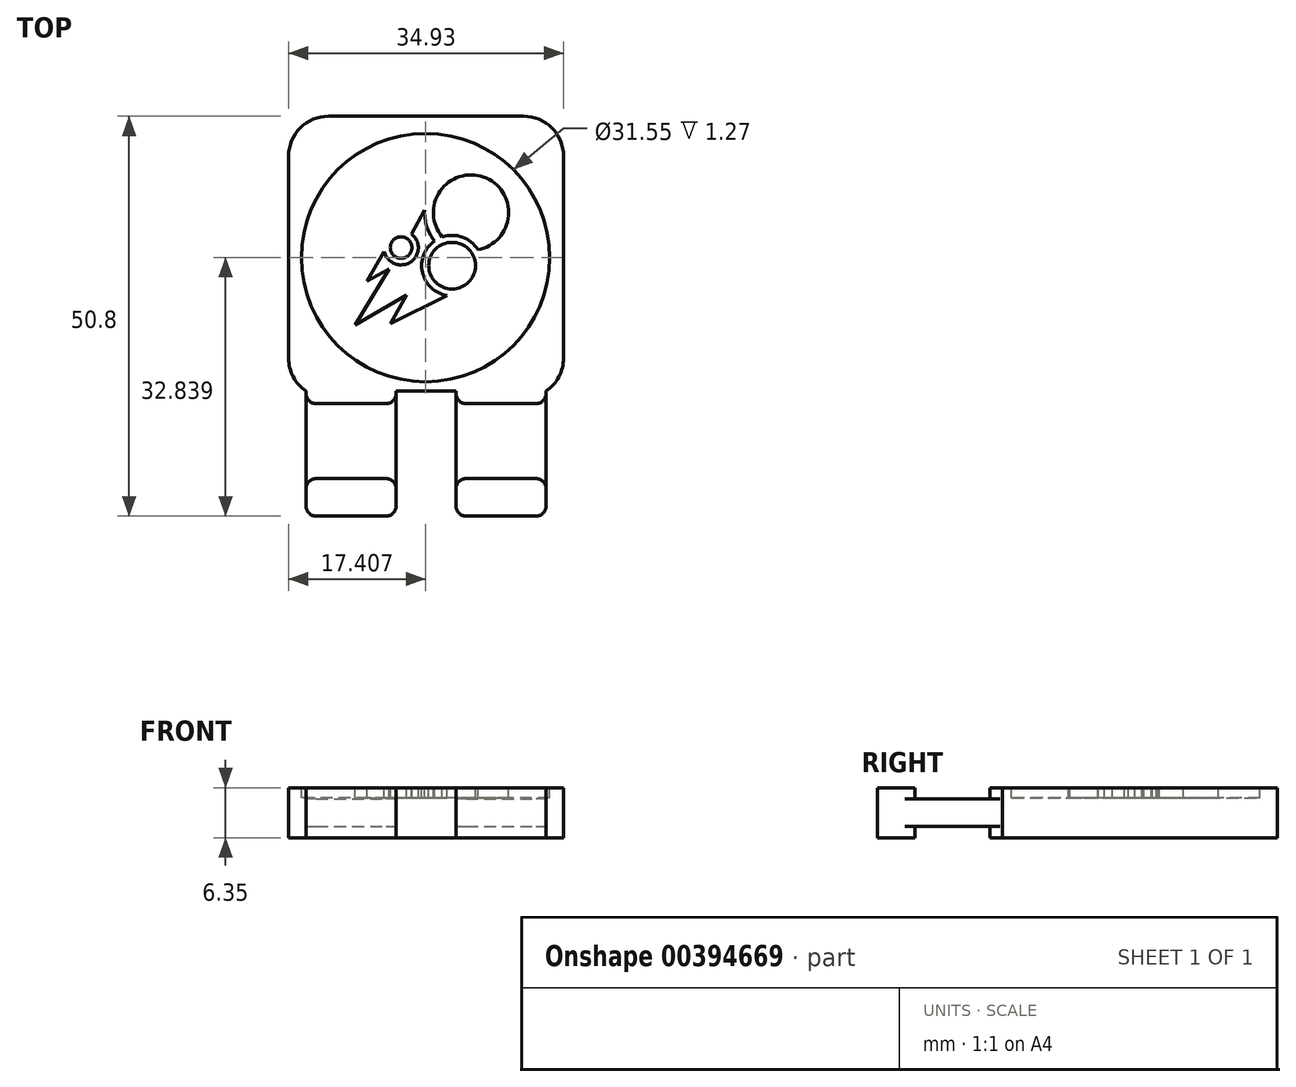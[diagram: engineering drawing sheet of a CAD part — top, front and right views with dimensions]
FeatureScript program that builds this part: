
annotation { "Feature Type Name" : "Feature", "Feature Type Description" : "" }
export const myFeature = defineFeature(function(context is Context, id is Id, definition is map)
    precondition{}
    {
        {
            var Q0;
            Q0=qCreatedBy(makeId("Top.planeOp"),FACE);
            var sketch = newSketch(context, id + "F0", { "sketchPlane" : qUnion([Q0])});
            skLineSegment(sketch, "E0.bottom", {"start": v(-17.15, 21.98) * mm, "end": v(17.78, 21.98) * mm});
            skLineSegment(sketch, "E0.top", {"start": v(-14.92, -28.82) * mm, "end": v(-3.5, -28.82) * mm});
            skLineSegment(sketch, "E0.left", {"start": v(-17.15, 21.98) * mm, "end": v(-17.15, -12.94) * mm});
            skLineSegment(sketch, "E0.right", {"start": v(17.78, 21.98) * mm, "end": v(17.78, -12.94) * mm});
            skPoint(sketch, "E0.middle", {"position": v(0, 0) * mm});
            skLineSegment(sketch, "E1", {"start": v(-17.15, -12.94) * mm, "end": v(-14.92, -12.94) * mm});
            skLineSegment(sketch, "E2", {"start": v(-14.92, -12.94) * mm, "end": v(-14.92, -28.82) * mm});
            skLineSegment(sketch, "E3", {"start": v(-3.5, -28.82) * mm, "end": v(-3.5, -12.94) * mm});
            skLineSegment(sketch, "E4", {"start": v(-3.5, -12.94) * mm, "end": v(4.13, -12.94) * mm});
            skLineSegment(sketch, "E5", {"start": v(4.13, -12.94) * mm, "end": v(4.13, -28.82) * mm});
            skLineSegment(sketch, "E6", {"start": v(17.78, -12.94) * mm, "end": v(15.56, -12.94) * mm});
            skLineSegment(sketch, "E7", {"start": v(15.56, -12.94) * mm, "end": v(15.56, -28.82) * mm});
            skLineSegment(sketch, "E8.trimOffspring", {"start": v(4.13, -28.82) * mm, "end": v(15.56, -28.82) * mm});
            skSolve(sketch);
        }
        {
            var Q0;
            Q0 = qSketchRegion(id + "F0", true);
            extrude(context, id + "F1", {"entities" : qUnion([Q0]), "endBound" : BoundingType.SYMMETRIC, "depth" : 6.35 * mm});
        }
        {
            var Q0;
            Q0=qCreatedBy(makeId("Right.planeOp"),FACE);
            var sketch = newSketch(context, id + "F2", { "sketchPlane" : qUnion([Q0])});
            skLineSegment(sketch, "E9", {"start": v(-14.53, -1.73) * mm, "end": v(-24.05, -1.73) * mm});
            skLineSegment(sketch, "E10", {"start": v(-24.05, -1.73) * mm, "end": v(-24.05, -3.18) * mm});
            skLineSegment(sketch, "E11", {"start": v(-24.05, -3.18) * mm, "end": v(-14.53, -3.18) * mm});
            skLineSegment(sketch, "E12", {"start": v(-14.53, 1.73) * mm, "end": v(-24.05, 1.73) * mm});
            skLineSegment(sketch, "E13", {"start": v(-24.05, 1.73) * mm, "end": v(-24.05, 3.18) * mm});
            skLineSegment(sketch, "E14", {"start": v(-24.05, 3.18) * mm, "end": v(-14.53, 3.18) * mm});
            skLineSegment(sketch, "E15", {"start": v(-14.53, 1.73) * mm, "end": v(-14.53, 3.18) * mm});
            skLineSegment(sketch, "E16", {"start": v(-14.53, -3.18) * mm, "end": v(-14.53, -1.73) * mm});
            skSolve(sketch);
        }
        {
            var Q0;
            Q0 = qSketchRegion(id + "F2", true);
            extrude(context, id + "F3", {"entities" : qUnion([Q0]), "operationType" : NewBodyOperationType.REMOVE, "endBound" : BoundingType.SYMMETRIC, "oppositeDirection" : true, "depth" : 50.8 * mm});
        }
        {
            var Q0;
            {var subQ0=sQuery(id+"F0.wireOp",EDGE,"E1");var subQ1=sQuery(id+"F0.wireOp",EDGE,"E0.left");var subQ2=sQuery(id+"F0.wireOp",EDGE,"E0.right");var subQ3=sQuery(id+"F0.wireOp",EDGE,"E0.bottom");var subQ4=sQuery(id+"F0.wireOp",EDGE,"E6");var subQ5=sQuery(id+"F0.wireOp",EDGE,"E4");Q0=makeQuery(id+"F3.boolean.opBoolean","SPLIT",FACE,{"disambiguationData":[TD([makeQuery(id+"F1.opExtrude","SWEPT_FACE",FACE,{"disambiguationData":[OSD([subQ3])]})])],"derivedFrom":makeQuery(id+"F1.opExtrude","CAP_FACE",FACE,{"disambiguationData":[OSD([subQ3,sQuery(id+"F0.wireOp",EDGE,"E0.top"),subQ1,subQ2,subQ0,sQuery(id+"F0.wireOp",EDGE,"E2"),sQuery(id+"F0.wireOp",EDGE,"E3"),subQ5,sQuery(id+"F0.wireOp",EDGE,"E5"),subQ4,sQuery(id+"F0.wireOp",EDGE,"E7"),sQuery(id+"F0.wireOp",EDGE,"E8.trimOffspring")])],"isStart":false})});}
            var sketch = newSketch(context, id + "F4", { "sketchPlane" : qUnion([Q0])});
            skPoint(sketch, "E17", {"position": v(-17.15, 4.52) * mm});
            skArc(sketch, "E18", {"start": v(6.9, 5.03) * mm, "mid": v(7.65, 14.25) * mm, "end": v(2.38, 6.65) * mm});
            skCircle(sketch, "E19", {"center": v(3.62, 3) * mm, "radius": 2.97 * mm});
            skCircle(sketch, "E20", {"center": v(-2.86, 5.3) * mm, "radius": 1.37 * mm});
            skArc(sketch, "E21", {"start": v(0.15, 10.05) * mm, "mid": v(0.4, 7.98) * mm, "end": v(1.38, 6.13) * mm});
            skArc(sketch, "E22", {"start": v(6.9, 5.03) * mm, "mid": v(4.92, 6.62) * mm, "end": v(2.38, 6.65) * mm});
            skArc(sketch, "E23", {"start": v(-5, 4.82) * mm, "mid": v(-1.68, 3.44) * mm, "end": v(-1.5, 7.03) * mm});
            skLineSegment(sketch, "E24", {"start": v(-7.2, 1.03) * mm, "end": v(-5, 4.82) * mm});
            skLineSegment(sketch, "E25", {"start": v(-7.2, 1.03) * mm, "end": v(-4.38, 2.58) * mm});
            skLineSegment(sketch, "E26", {"start": v(-4.38, 2.58) * mm, "end": v(-8.68, -4.53) * mm});
            skLineSegment(sketch, "E27", {"start": v(-8.68, -4.53) * mm, "end": v(-2.16, -0.76) * mm});
            skLineSegment(sketch, "E28", {"start": v(-2.16, -0.76) * mm, "end": v(-4.22, -4.33) * mm});
            skLineSegment(sketch, "E29", {"start": v(-4.22, -4.33) * mm, "end": v(2.95, -0.8) * mm});
            skLineSegment(sketch, "E30.trimOffspring", {"start": v(-1.5, 7.03) * mm, "end": v(0.15, 10.05) * mm});
            skArc(sketch, "E31.trimOffspring", {"start": v(1.38, 6.13) * mm, "mid": v(-0.14, 2.14) * mm, "end": v(2.95, -0.8) * mm});
            skLineSegment(sketch, "E32", {"start": v(-17.15, 21.98) * mm, "end": v(17.78, 21.98) * mm});
            skLineSegment(sketch, "E33", {"start": v(17.78, 21.98) * mm, "end": v(17.78, -12.94) * mm});
            skLineSegment(sketch, "E34", {"start": v(17.78, -12.94) * mm, "end": v(-17.15, -12.94) * mm});
            skLineSegment(sketch, "E35", {"start": v(-17.15, 21.98) * mm, "end": v(-17.15, -12.94) * mm});
            skCircle(sketch, "E36", {"center": v(0.26, 4.02) * mm, "radius": 15.77 * mm});
            skSolve(sketch);
        }
        {
            var Q0;
            Q0=makeQuery(id+"F4.imprint","IMPRINT",FACE,{"disambiguationData":[TD([[makeQuery(id+"F4.imprint","IMPRINT",EDGE,{"derivedFrom":sQuery(id+"F4.wireOp",EDGE,"E18")}),-1.0]])]});
            extrude(context, id + "F5", {"entities" : qUnion([Q0]), "operationType" : NewBodyOperationType.REMOVE, "oppositeDirection" : true, "offsetDistance" : 25.4 * mm, "depth" : 1.27 * mm});
        }
        {
            var Q0;
            Q0=makeQuery(id+"F1.opExtrude","SWEPT_EDGE",EDGE,{"disambiguationData":[OSD([sQuery(id+"F0.wireOp",EDGE,"E0.bottom"),sQuery(id+"F0.wireOp",EDGE,"E0.right")])]});
            var Q1;
            Q1=makeQuery(id+"F1.opExtrude","SWEPT_EDGE",EDGE,{"disambiguationData":[OSD([sQuery(id+"F0.wireOp",EDGE,"E0.left"),sQuery(id+"F0.wireOp",EDGE,"E1")])]});
            var Q2;
            Q2=makeQuery(id+"F1.opExtrude","SWEPT_EDGE",EDGE,{"disambiguationData":[OSD([sQuery(id+"F0.wireOp",EDGE,"E0.right"),sQuery(id+"F0.wireOp",EDGE,"E6")])]});
            var Q3;
            Q3=makeQuery(id+"F1.opExtrude","SWEPT_EDGE",EDGE,{"disambiguationData":[OSD([sQuery(id+"F0.wireOp",EDGE,"E0.bottom"),sQuery(id+"F0.wireOp",EDGE,"E0.left")])]});
            fillet(context, id + "F6", {"entities" : qUnion([Q0, Q1, Q2, Q3]), "radius" : 5.08 * mm, "tangentPropagation" : true, "allowEdgeOverflow" : false});
        }
        {
            var Q0;
            {var subQ0=makeQuery(id+"F3.opExtrude","SWEPT_FACE",FACE,{"disambiguationData":[OSD([sQuery(id+"F2.wireOp",EDGE,"x62yvcTG-1TIA-uCk9-cSXU-WGpYtcgAMLtR")])]});var subQ1=makeQuery(id+"F3.opExtrude","SWEPT_FACE",FACE,{"disambiguationData":[OSD([sQuery(id+"F2.wireOp",EDGE,"bjkGccF4-ztdF-G65M-RJ6u-XlurXhTa0Hjr")])]});Q0=makeQuery(id+"F6.opFillet","BLEND_EDGE",EDGE,{"blendedFrom":[makeQuery(id+"F3.boolean.opBoolean","INTERSECT",EDGE,{"disambiguationData":[topologyDisambiguationEdgeConnected([makeQuery(id+"F1.opExtrude","SWEPT_FACE",FACE,{"disambiguationData":[OSD([sQuery(id+"F0.wireOp",EDGE,"E0.right")])]})])],"derivedFrom":[subQ0,subQ1]}),makeQuery(id+"F1.opExtrude","SWEPT_FACE",FACE,{"disambiguationData":[OSD([sQuery(id+"F0.wireOp",EDGE,"E7")])]})],"blendedInto":[makeQuery(id+"F1.opExtrude","SWEPT_FACE",FACE,{"disambiguationData":[OSD([sQuery(id+"F0.wireOp",EDGE,"E7")])]})]});}
            var Q1;
            {var subQ0=makeQuery(id+"F3.opExtrude","SWEPT_FACE",FACE,{"disambiguationData":[OSD([sQuery(id+"F2.wireOp",EDGE,"x62yvcTG-1TIA-uCk9-cSXU-WGpYtcgAMLtR")])]});var subQ1=makeQuery(id+"F3.opExtrude","SWEPT_FACE",FACE,{"disambiguationData":[OSD([sQuery(id+"F2.wireOp",EDGE,"bjkGccF4-ztdF-G65M-RJ6u-XlurXhTa0Hjr")])]});Q1=makeQuery(id+"F6.opFillet","BLEND_EDGE",EDGE,{"blendedFrom":[makeQuery(id+"F3.boolean.opBoolean","INTERSECT",EDGE,{"disambiguationData":[topologyDisambiguationEdgeConnected([makeQuery(id+"F1.opExtrude","SWEPT_FACE",FACE,{"disambiguationData":[OSD([sQuery(id+"F0.wireOp",EDGE,"E0.left")])]})])],"derivedFrom":[subQ0,subQ1]}),makeQuery(id+"F1.opExtrude","SWEPT_FACE",FACE,{"disambiguationData":[OSD([sQuery(id+"F0.wireOp",EDGE,"E2")])]})],"blendedInto":[makeQuery(id+"F1.opExtrude","SWEPT_FACE",FACE,{"disambiguationData":[OSD([sQuery(id+"F0.wireOp",EDGE,"E2")])]})]});}
            var Q2;
            Q2=makeQuery(id+"F3.boolean.opBoolean","INTERSECT",EDGE,{"derivedFrom":[makeQuery(id+"F1.opExtrude","SWEPT_FACE",FACE,{"disambiguationData":[OSD([sQuery(id+"F0.wireOp",EDGE,"E2")])]}),makeQuery(id+"F3.opExtrude","SWEPT_FACE",FACE,{"disambiguationData":[OSD([sQuery(id+"F2.wireOp",EDGE,"E15")])]})]});
            var Q3;
            Q3=makeQuery(id+"F3.boolean.opBoolean","INTERSECT",EDGE,{"derivedFrom":[makeQuery(id+"F1.opExtrude","SWEPT_FACE",FACE,{"disambiguationData":[OSD([sQuery(id+"F0.wireOp",EDGE,"E3")])]}),makeQuery(id+"F3.opExtrude","SWEPT_FACE",FACE,{"disambiguationData":[OSD([sQuery(id+"F2.wireOp",EDGE,"E15")])]})]});
            var Q4;
            Q4=makeQuery(id+"F3.boolean.opBoolean","INTERSECT",EDGE,{"derivedFrom":[makeQuery(id+"F1.opExtrude","SWEPT_FACE",FACE,{"disambiguationData":[OSD([sQuery(id+"F0.wireOp",EDGE,"E7")])]}),makeQuery(id+"F3.opExtrude","SWEPT_FACE",FACE,{"disambiguationData":[OSD([sQuery(id+"F2.wireOp",EDGE,"E15")])]})]});
            var Q5;
            Q5=makeQuery(id+"F3.boolean.opBoolean","INTERSECT",EDGE,{"derivedFrom":[makeQuery(id+"F1.opExtrude","SWEPT_FACE",FACE,{"disambiguationData":[OSD([sQuery(id+"F0.wireOp",EDGE,"E5")])]}),makeQuery(id+"F3.opExtrude","SWEPT_FACE",FACE,{"disambiguationData":[OSD([sQuery(id+"F2.wireOp",EDGE,"E15")])]})]});
            var Q6;
            Q6=makeQuery(id+"F3.boolean.opBoolean","INTERSECT",EDGE,{"derivedFrom":[makeQuery(id+"F1.opExtrude","SWEPT_FACE",FACE,{"disambiguationData":[OSD([sQuery(id+"F0.wireOp",EDGE,"E7")])]}),makeQuery(id+"F3.opExtrude","SWEPT_FACE",FACE,{"disambiguationData":[OSD([sQuery(id+"F2.wireOp",EDGE,"E16")])]})]});
            var Q7;
            Q7=makeQuery(id+"F3.boolean.opBoolean","INTERSECT",EDGE,{"derivedFrom":[makeQuery(id+"F1.opExtrude","SWEPT_FACE",FACE,{"disambiguationData":[OSD([sQuery(id+"F0.wireOp",EDGE,"E5")])]}),makeQuery(id+"F3.opExtrude","SWEPT_FACE",FACE,{"disambiguationData":[OSD([sQuery(id+"F2.wireOp",EDGE,"E16")])]})]});
            var Q8;
            Q8=makeQuery(id+"F3.boolean.opBoolean","INTERSECT",EDGE,{"derivedFrom":[makeQuery(id+"F1.opExtrude","SWEPT_FACE",FACE,{"disambiguationData":[OSD([sQuery(id+"F0.wireOp",EDGE,"E2")])]}),makeQuery(id+"F3.opExtrude","SWEPT_FACE",FACE,{"disambiguationData":[OSD([sQuery(id+"F2.wireOp",EDGE,"E16")])]})]});
            var Q9;
            Q9=makeQuery(id+"F3.boolean.opBoolean","INTERSECT",EDGE,{"derivedFrom":[makeQuery(id+"F1.opExtrude","SWEPT_FACE",FACE,{"disambiguationData":[OSD([sQuery(id+"F0.wireOp",EDGE,"E3")])]}),makeQuery(id+"F3.opExtrude","SWEPT_FACE",FACE,{"disambiguationData":[OSD([sQuery(id+"F2.wireOp",EDGE,"E16")])]})]});
            var Q10;
            Q10=makeQuery(id+"F3.boolean.opBoolean","INTERSECT",EDGE,{"derivedFrom":[makeQuery(id+"F1.opExtrude","SWEPT_FACE",FACE,{"disambiguationData":[OSD([sQuery(id+"F0.wireOp",EDGE,"E3")])]}),makeQuery(id+"F3.opExtrude","SWEPT_FACE",FACE,{"disambiguationData":[OSD([sQuery(id+"F2.wireOp",EDGE,"E10")])]})]});
            var Q11;
            Q11=makeQuery(id+"F3.boolean.opBoolean","INTERSECT",EDGE,{"derivedFrom":[makeQuery(id+"F1.opExtrude","SWEPT_FACE",FACE,{"disambiguationData":[OSD([sQuery(id+"F0.wireOp",EDGE,"E3")])]}),makeQuery(id+"F3.opExtrude","SWEPT_FACE",FACE,{"disambiguationData":[OSD([sQuery(id+"F2.wireOp",EDGE,"E13")])]})]});
            var Q12;
            Q12=makeQuery(id+"F3.boolean.opBoolean","INTERSECT",EDGE,{"derivedFrom":[makeQuery(id+"F1.opExtrude","SWEPT_FACE",FACE,{"disambiguationData":[OSD([sQuery(id+"F0.wireOp",EDGE,"E7")])]}),makeQuery(id+"F3.opExtrude","SWEPT_FACE",FACE,{"disambiguationData":[OSD([sQuery(id+"F2.wireOp",EDGE,"E10")])]})]});
            var Q13;
            Q13=makeQuery(id+"F3.boolean.opBoolean","INTERSECT",EDGE,{"derivedFrom":[makeQuery(id+"F1.opExtrude","SWEPT_FACE",FACE,{"disambiguationData":[OSD([sQuery(id+"F0.wireOp",EDGE,"E7")])]}),makeQuery(id+"F3.opExtrude","SWEPT_FACE",FACE,{"disambiguationData":[OSD([sQuery(id+"F2.wireOp",EDGE,"E13")])]})]});
            var Q14;
            Q14=makeQuery(id+"F1.opExtrude","SWEPT_EDGE",EDGE,{"disambiguationData":[OSD([sQuery(id+"F0.wireOp",EDGE,"E7"),sQuery(id+"F0.wireOp",EDGE,"E8.trimOffspring")])]});
            var Q15;
            Q15=makeQuery(id+"F1.opExtrude","SWEPT_EDGE",EDGE,{"disambiguationData":[OSD([sQuery(id+"F0.wireOp",EDGE,"E5"),sQuery(id+"F0.wireOp",EDGE,"E8.trimOffspring")])]});
            var Q16;
            Q16=makeQuery(id+"F1.opExtrude","SWEPT_EDGE",EDGE,{"disambiguationData":[OSD([sQuery(id+"F0.wireOp",EDGE,"E0.top"),sQuery(id+"F0.wireOp",EDGE,"E3")])]});
            var Q17;
            Q17=makeQuery(id+"F1.opExtrude","SWEPT_EDGE",EDGE,{"disambiguationData":[OSD([sQuery(id+"F0.wireOp",EDGE,"E0.top"),sQuery(id+"F0.wireOp",EDGE,"E2")])]});
            var Q18;
            Q18=makeQuery(id+"F3.boolean.opBoolean","INTERSECT",EDGE,{"derivedFrom":[makeQuery(id+"F1.opExtrude","SWEPT_FACE",FACE,{"disambiguationData":[OSD([sQuery(id+"F0.wireOp",EDGE,"E2")])]}),makeQuery(id+"F3.opExtrude","SWEPT_FACE",FACE,{"disambiguationData":[OSD([sQuery(id+"F2.wireOp",EDGE,"E13")])]})]});
            var Q19;
            Q19=makeQuery(id+"F3.boolean.opBoolean","INTERSECT",EDGE,{"derivedFrom":[makeQuery(id+"F1.opExtrude","SWEPT_FACE",FACE,{"disambiguationData":[OSD([sQuery(id+"F0.wireOp",EDGE,"E2")])]}),makeQuery(id+"F3.opExtrude","SWEPT_FACE",FACE,{"disambiguationData":[OSD([sQuery(id+"F2.wireOp",EDGE,"E10")])]})]});
            var Q20;
            Q20=makeQuery(id+"F3.boolean.opBoolean","INTERSECT",EDGE,{"derivedFrom":[makeQuery(id+"F1.opExtrude","SWEPT_FACE",FACE,{"disambiguationData":[OSD([sQuery(id+"F0.wireOp",EDGE,"E5")])]}),makeQuery(id+"F3.opExtrude","SWEPT_FACE",FACE,{"disambiguationData":[OSD([sQuery(id+"F2.wireOp",EDGE,"E13")])]})]});
            var Q21;
            Q21=makeQuery(id+"F3.boolean.opBoolean","INTERSECT",EDGE,{"derivedFrom":[makeQuery(id+"F1.opExtrude","SWEPT_FACE",FACE,{"disambiguationData":[OSD([sQuery(id+"F0.wireOp",EDGE,"E5")])]}),makeQuery(id+"F3.opExtrude","SWEPT_FACE",FACE,{"disambiguationData":[OSD([sQuery(id+"F2.wireOp",EDGE,"E10")])]})]});
            fillet(context, id + "F7", {"entities" : qUnion([Q0, Q1, Q2, Q3, Q4, Q5, Q6, Q7, Q8, Q9, Q10, Q11, Q12, Q13, Q14, Q15, Q16, Q17, Q18, Q19, Q20, Q21]), "radius" : 1.27 * mm, "tangentPropagation" : true, "allowEdgeOverflow" : false});
        }
    });
